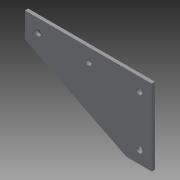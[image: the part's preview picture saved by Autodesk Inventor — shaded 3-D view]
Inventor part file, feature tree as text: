
AUTODESK INVENTOR PART (.ipt)
format: ipt  version: 2013 (Build 170138000, 138)  size: 106,496 bytes
history: native  units: in
note: dims shown in document units (in); Inventor stores cm internally (conversion verified against a paired STEP export)
features: extrude x2, sketch x2, plane x1
ambient origin geometry x8: Origin, YZ Plane, XZ Plane, XY Plane, X Axis, Y Axis, Z Axis, Center Point
bodies: Solid1 (feature_tree)
feature tree (5):
  plane  "Work Plane1"
  extrude  "Extrusion1"  Depth=1.0in
  extrude  "Extrusion2"  Depth=1.0in
  sketch  "Sketch1"  dims[d0=26.5in d1=1.0in]
  sketch  "Sketch2"  dims[d2=10.0in d3=1.0in d4=1.0in d5=5.0in d6=5.0in d7=1.0in d14=0.25in d15=0.25in d16=0.25in d17=0.25in d20=0.25in d21=0.125in d22=0.0in d23=1.0in d24=3.0in d25=1.0in d26=0.0in]
